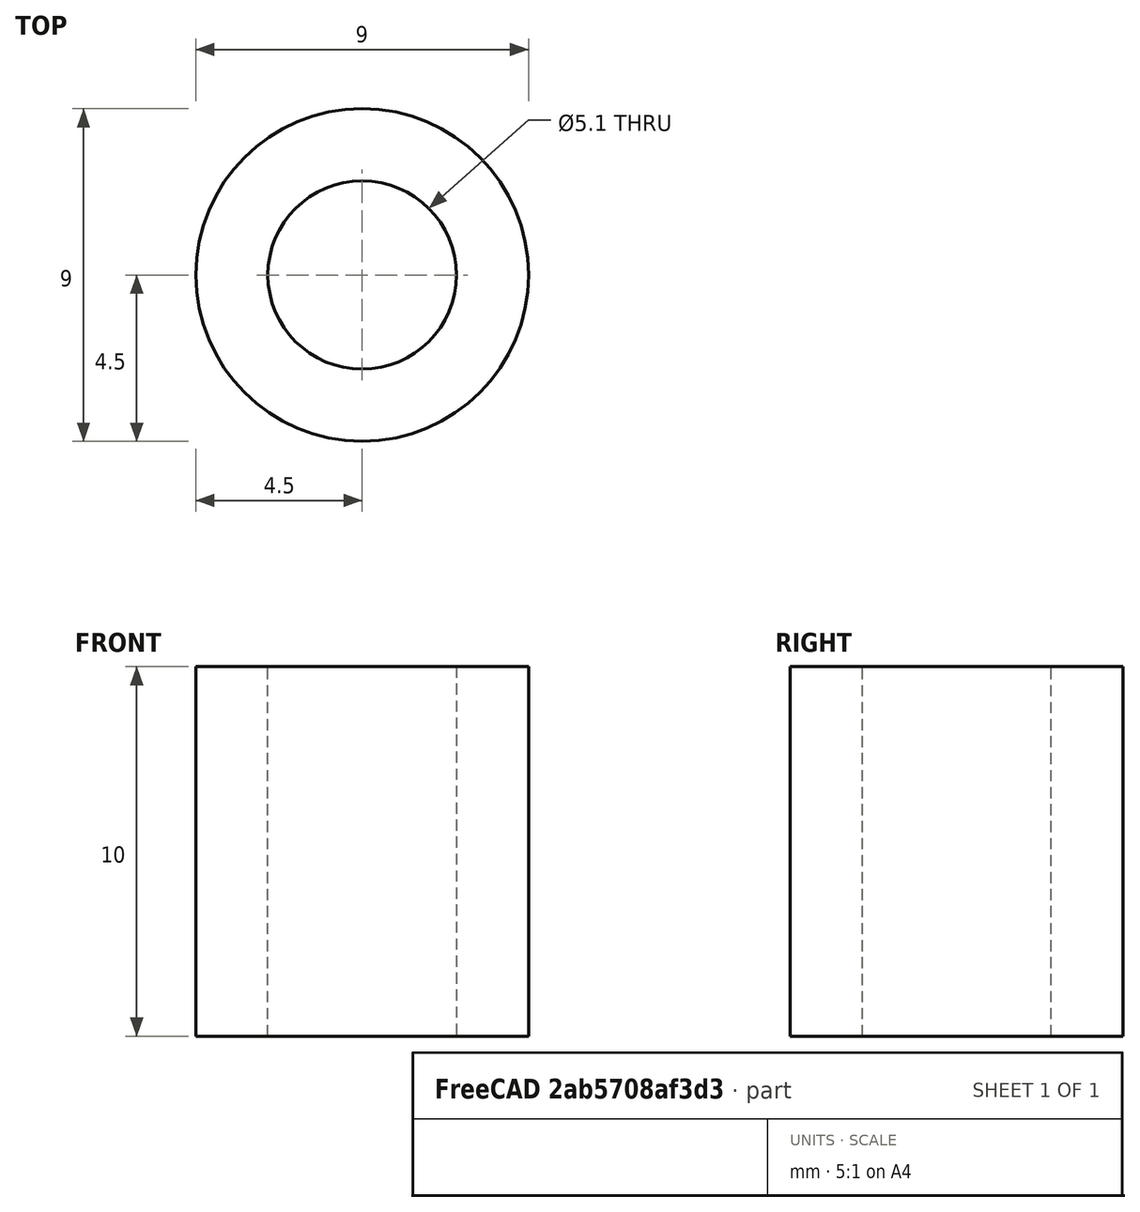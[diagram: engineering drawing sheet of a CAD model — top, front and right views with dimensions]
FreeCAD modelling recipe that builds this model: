
FCSTD DOCUMENT  (FreeCAD 0.17R10495 (Git))
Label: spacer_xlong
License: All rights reserved
LicenseURL: http://en.wikipedia.org/wiki/All_rights_reserved
objects: Part::Cylinder×1, PartDesign::ShapeBinder×1, Sketcher::SketchObject×1, PartDesign::Pocket×1, PartDesign::Body×1
note: 6 computed .brp shape members not serialized (recipe doc carries the construction recipe); baked Part::Feature solids carry a one-line shape summary decoded from their .brp

FEATURE [Part::Cylinder] Cylinder
  Angle = 360
  AttacherType = Attacher::AttachEngine3D
  Height = 10
  Placement = pos=(-26,22,0) rot=(0,0,1;0rad)
  Radius = 4.5
FEATURE [PartDesign::ShapeBinder] CopyCylinder
  Placement = pos=(-26,22,0) rot=(0,0,1;0rad)
FEATURE [Sketcher::SketchObject] Sketch002
  MapMode = 5
  Placement = pos=(-26,22,11) rot=(0,0,1;0rad)
  Support = -> [CopyCylinder]
  sketch-geometry (1):
    g0: Circle CenterX=0 CenterY=0 CenterZ=0 NormalX=0 NormalY=0 NormalZ=1 Radius=2.55
  constraints (2):
    c: Coincident(g0,g-1)
    c: Radius(g0) = 2.55
FEATURE [PartDesign::Pocket] Pocket001
  BaseFeature = -> Cylinder
  Length = 5
  Placement = pos=(-26,22,0) rot=(0,0,1;0rad)
  Profile = -> Sketch002
  Type = 1
FEATURE [PartDesign::Body] Body001  label="spacer_long"
  BaseFeature = -> Cylinder
  Group = -> [CopyCylinder,Sketch002,Pocket001]
  Origin = -> Body001Origin
  Tip = -> Pocket001
